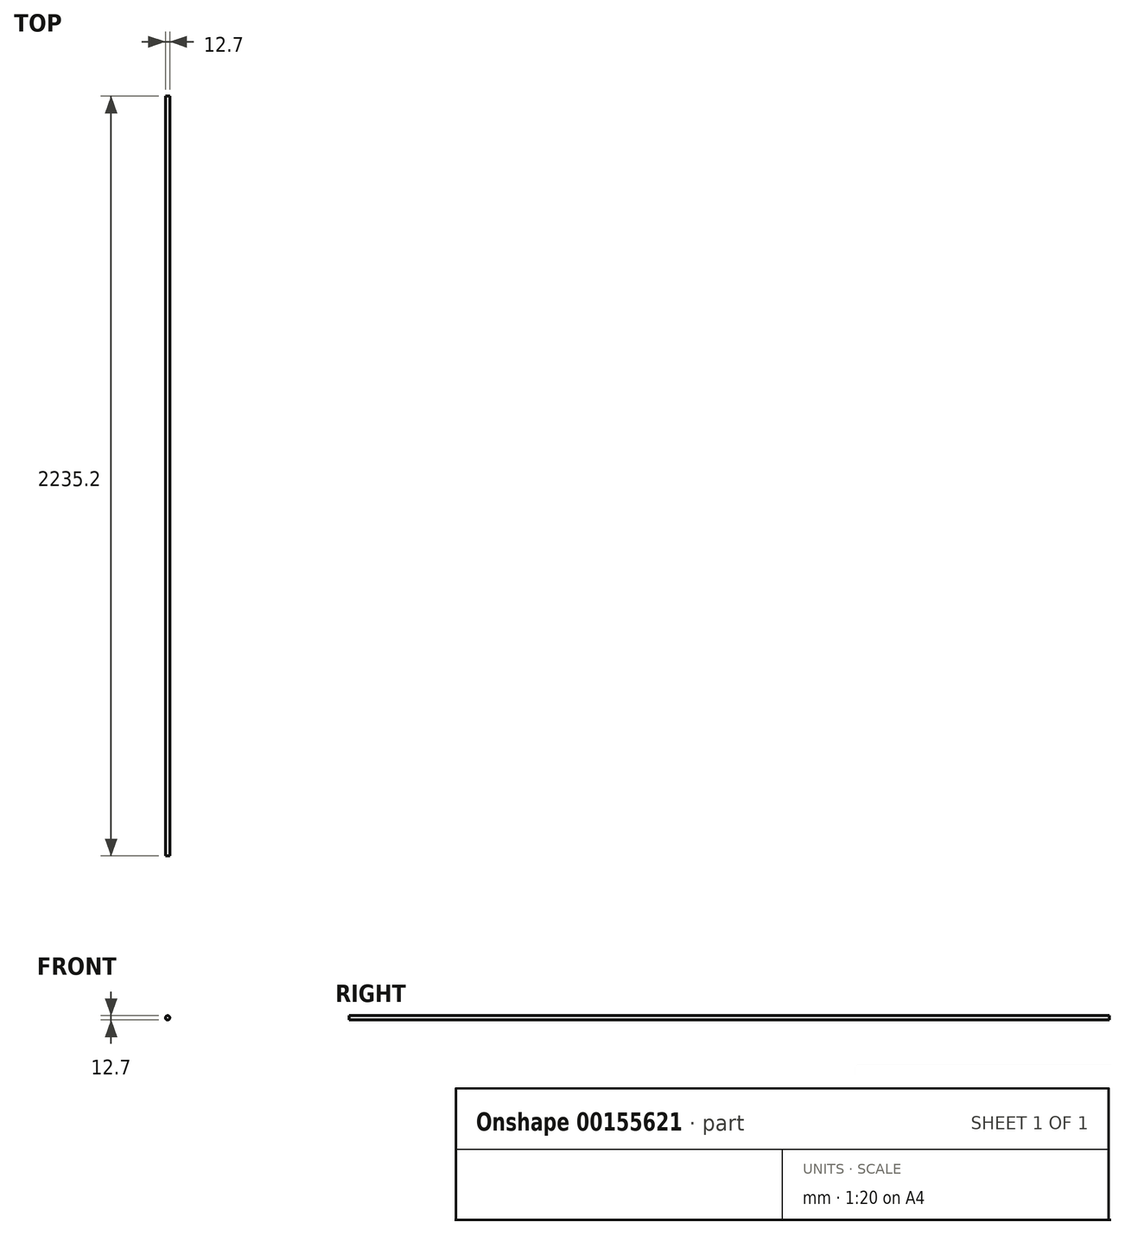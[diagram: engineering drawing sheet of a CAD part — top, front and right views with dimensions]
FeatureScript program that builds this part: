
annotation { "Feature Type Name" : "Feature", "Feature Type Description" : "" }
export const myFeature = defineFeature(function(context is Context, id is Id, definition is map)
    precondition{}
    {
        {
            var Q0;
            Q0=qCreatedBy(makeId("Front.planeOp"),FACE);
            var sketch = newSketch(context, id + "F0", { "sketchPlane" : qUnion([Q0])});
            skCircle(sketch, "E0", {"center": v(0, 0) * mm, "radius": 6.35 * mm});
            skSolve(sketch);
        }
        {
            var Q0;
            Q0 = qSketchRegion(id + "F0", true);
            extrude(context, id + "F1", {"entities" : qUnion([Q0]), "depth" : 2235.2 * mm});
        }
    });
